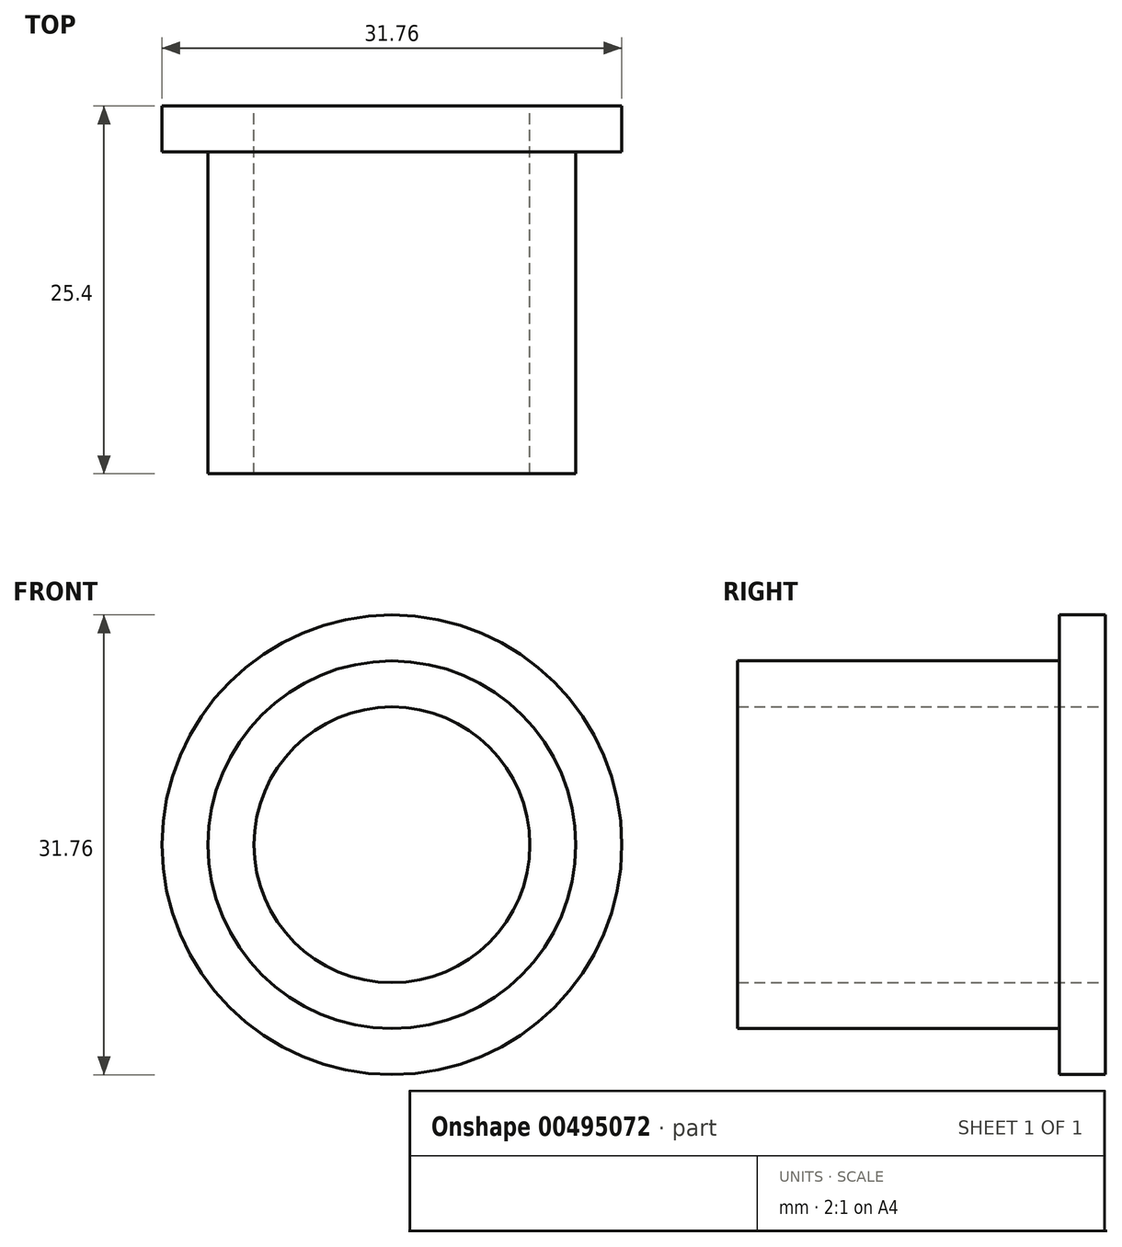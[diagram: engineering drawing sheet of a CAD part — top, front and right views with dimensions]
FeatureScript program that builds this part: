
annotation { "Feature Type Name" : "Feature", "Feature Type Description" : "" }
export const myFeature = defineFeature(function(context is Context, id is Id, definition is map)
    precondition{}
    {
        {
            var Q0;
            Q0=qCreatedBy(makeId("Front.planeOp"),FACE);
            var sketch = newSketch(context, id + "F0", { "sketchPlane" : qUnion([Q0])});
            skCircle(sketch, "E0", {"center": v(0, 0) * mm, "radius": 15.88 * mm});
            skSolve(sketch);
        }
        {
            var Q0;
            Q0=makeQuery(id+"F0.imprint","IMPRINT",FACE,{"disambiguationData":[TD([[makeQuery(id+"F0.imprint","IMPRINT",EDGE,{"derivedFrom":sQuery(id+"F0.wireOp",EDGE,"E0")}),1.0]])]});
            var sketch = newSketch(context, id + "F1", { "sketchPlane" : qUnion([Q0])});
            skCircle(sketch, "E1", {"center": v(0, 0) * mm, "radius": 12.7 * mm});
            skSolve(sketch);
        }
        {
            var Q0;
            Q0=makeQuery(id+"F0.imprint","IMPRINT",FACE,{"disambiguationData":[TD([[makeQuery(id+"F0.imprint","IMPRINT",EDGE,{"derivedFrom":sQuery(id+"F0.wireOp",EDGE,"E0")}),1.0]])]});
            var sketch = newSketch(context, id + "F2", { "sketchPlane" : qUnion([Q0])});
            skCircle(sketch, "E2", {"center": v(0, 0) * mm, "radius": 9.53 * mm});
            skSolve(sketch);
        }
        {
            var Q0;
            Q0=makeQuery(id+"F1.imprint","IMPRINT",FACE,{"disambiguationData":[TD([[makeQuery(id+"F1.imprint","IMPRINT",EDGE,{"derivedFrom":sQuery(id+"F1.wireOp",EDGE,"E1")}),1.0]])]});
            extrude(context, id + "F3", {"entities" : qUnion([Q0]), "depth" : 25.4 * mm});
        }
        {
            var Q0;
            Q0=makeQuery(id+"F0.imprint","IMPRINT",FACE,{"disambiguationData":[TD([[makeQuery(id+"F0.imprint","IMPRINT",EDGE,{"derivedFrom":sQuery(id+"F0.wireOp",EDGE,"E0")}),1.0]])]});
            extrude(context, id + "F4", {"entities" : qUnion([Q0]), "operationType" : NewBodyOperationType.ADD, "depth" : 3.17 * mm});
        }
        {
            var Q0;
            Q0=makeQuery(id+"F2.imprint","IMPRINT",FACE,{"disambiguationData":[TD([[makeQuery(id+"F2.imprint","IMPRINT",EDGE,{"derivedFrom":sQuery(id+"F2.wireOp",EDGE,"E2")}),1.0]])]});
            extrude(context, id + "F5", {"entities" : qUnion([Q0]), "operationType" : NewBodyOperationType.REMOVE, "endBound" : BoundingType.THROUGH_ALL, "depth" : 25.4 * mm});
        }
    });
